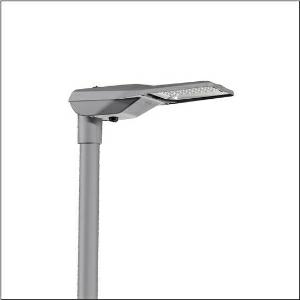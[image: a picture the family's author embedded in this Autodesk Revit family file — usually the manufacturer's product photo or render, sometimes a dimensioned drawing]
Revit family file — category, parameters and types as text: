
# Revit family: streetlight_sl_21_iq_mini___st1_0a_5xe2d21y08gb_b3c5
name_source: partatom
category: Lighting Fixtures
units: mm (PartAtom-declared; Revit-internal decimal feet)

## family parameters
Cut with Voids When Loaded = No
Host = Face
Light Source = No
Part Type = Normal
Room Calculation Point = No
Round Connector Dimension = Use Diameter
Shared = No

## types (1)
- --- (1 x LED, 4810 lm, 39.8 W, 2200K)
    Apparent Load = 40 VA
    CIE Flux Codes = 37 72 97 100 100
    Color Rendering = 70
    Color Temperature = 2200K
    Default Elevation = 1800 mm
    Description = Streetlight SL 21 iQ mini, mast luminaire, primary light control with lens, of PMMA, primary optical cover: cover, of toughened safety glass, transparent, light distribution: ST1.0a, light emission: direct distribution, primary light characteristic: asymmetric, installation type: post-top, side-entry, LED, High Power LED, rated luminous flux: 4.810lm, luminous efficacy: 121lm/W, light colour: 722, colour temperature: 2200K, control gear: iQ-Street Remote, D4i with power reduction, control: pre-setting: logarithmic dimming characteristic, Street-Remote, Auto-Match, Temp-Guard, Lumen-Switch, Night-Set, Smart-Wire, Light-Fading, Desk-Remote (wireless, voltage-free reading and setting of iQ features in the workshop via application-optimized NFC function/RFID function), optimised constant luminous flux control (CLO 2.0), mains connection: 220..240V, AC, 50/60Hz, start of lifetime: 40W, end of service life: 41W, reduction: 18W, luminaire housing, of diecast aluminium, powder-coated, SITECO metallic grey (DB 702S), corrosivity category C5 high according to DIN EN ISO 12944, please order mast flange separately, inclination adjustable: 0°, 5°, 10°, 15°, sealing non-destructively replaceable, multi-level sealing system, length: 628mm, width: 235mm, height: 110mm, mast flange for spigot size: 42mm (side-entry): 5XC10008XM4, 60/48mm (side-entry/post-top): 5XC10108XM2, 76/60mm (side-entry/post-top): 5XC10108XM1, mounting height: 4..8m, Smart Interface below and above, protection rating (complete): IP66, insulation class (complete): insulation class II (safety insulation), certification: CE, ENEC, ENEC+, VDE, impact resistance: IK10, permissible operating ambient temperature for outdoor applications: -40..+50°C, standard-compliant lighting for roads and squares, packaging unit: 1 piece

Light Distribution: ST1.0a
    Height = 110 mm
    Lamp = 1 x LED
    Lamp Light Flux = 4810 lm
    Lamp Power = 39.8 W
    Lamp count = 1
    Length = 625 mm
    Luminous efficacy = 121 lm/W
    Manufacturer = Siteco
    ModVariant = No
    Model = 5XE2D21Y08GB
    Number of Poles = 1
    OnlyDefault = Yes
    Power Factor = 1
    Product Name = Streetlight SL 21 iQ mini | ST1.0a
    Product group = mast luminaire | pylon top
    ProductGroupID = 6100
    Protection Class = Protection class II
    Protection Degree = IP 66
    RLX_Detail_Level = 1
    RLX_Emergency_Light_Flux = 0 lm
    RLX_Emergency_Type = 0
    RLX_Emergency_Type_DB = No
    RlxData = <blob elided: 93069 chars, md5=fe2d0eac>
    Socket = socket
    Standby Power = 0 W
    System Light Flux = 4810 lm
    System Power = 40 W
    Type Comments = factory setting: luminous flux: 100 % | dim-lin: 254 | 800 mA
    Type Image = l_1003514.jpg
    URL = http://relux.com
    VarID = @adj_115193
    Voltage = 0 V
    Weight = 0.00 kg
    Width = 234 mm

## geometry (parser evidence)
native form markers: Blend x4, Sweep x11
no freeform markers — native parametric forms only
